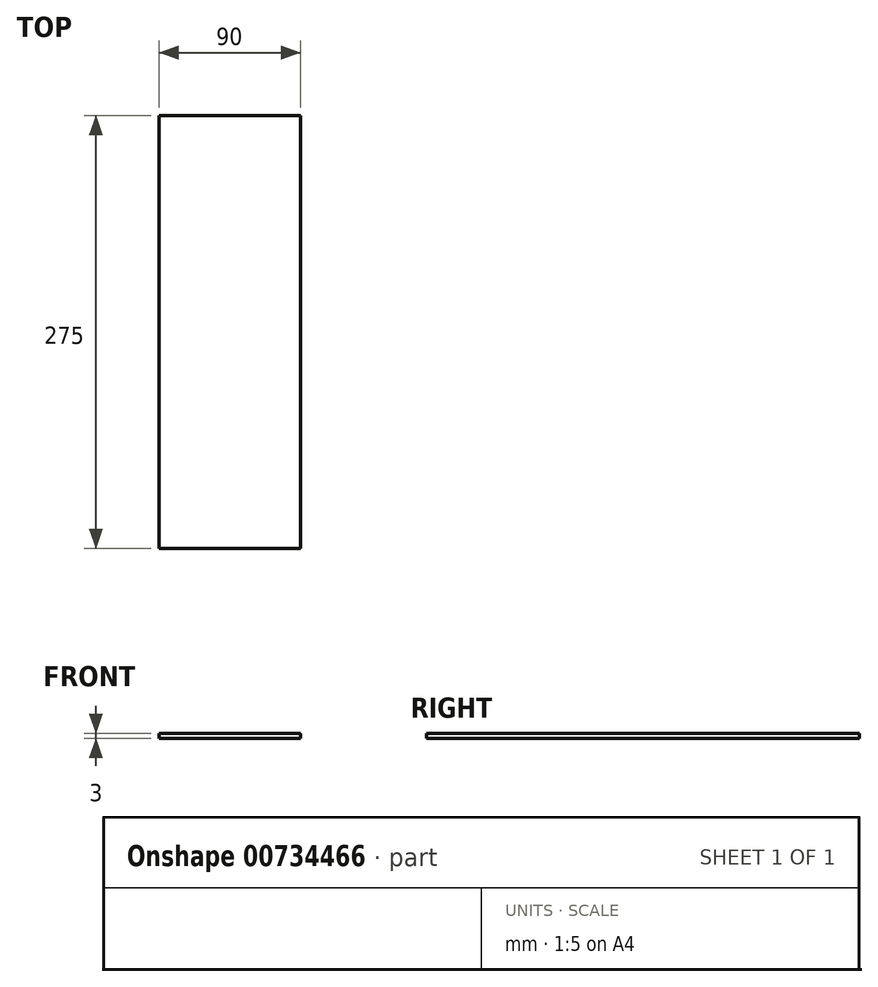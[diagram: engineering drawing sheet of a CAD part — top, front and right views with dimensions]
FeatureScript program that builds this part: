
annotation { "Feature Type Name" : "Feature", "Feature Type Description" : "" }
export const myFeature = defineFeature(function(context is Context, id is Id, definition is map)
    precondition{}
    {
        {
            var Q0;
            Q0=qCreatedBy(makeId("Front.planeOp"),FACE);
            var sketch = newSketch(context, id + "F0", { "sketchPlane" : qUnion([Q0])});
            skLineSegment(sketch, "E0", {"start": v(-50, 25) * mm, "end": v(50, 25) * mm});
            skLineSegment(sketch, "E1", {"start": v(50, 25) * mm, "end": v(50, -25) * mm});
            skLineSegment(sketch, "E2", {"start": v(-50, 25) * mm, "end": v(-50, -25) * mm});
            skSolve(sketch);
        }
        {
            var Q0;
            Q0=sQuery(id+"F0.wireOp",VERTEX,"E1.end");
            var Q1;
            Q1=qCreatedBy(makeId("Right.planeOp"),FACE);
            cPlane(context, id + "F1", {"entities" : qUnion([Q0, Q1]), "cplaneType" : CPlaneType.PLANE_POINT, "offset" : 25 * mm, "width" : 150 * mm, "height" : 150 * mm});
        }
        {
            var Q0;
            Q0=qCreatedBy(id+"F1.planeOp",FACE);
            var sketch = newSketch(context, id + "F2", { "sketchPlane" : qUnion([Q0])});
            skLineSegment(sketch, "E3", {"start": v(-20, -25) * mm, "end": v(20, -25) * mm});
            skSolve(sketch);
        }
        {
            var Q0;
            Q0=sQuery(id+"F0.wireOp",VERTEX,"E2.end");
            var Q1;
            Q1=qCreatedBy(makeId("Right.planeOp"),FACE);
            cPlane(context, id + "F3", {"entities" : qUnion([Q0, Q1]), "cplaneType" : CPlaneType.PLANE_POINT, "offset" : 25 * mm, "width" : 150 * mm, "height" : 150 * mm});
        }
        {
            var Q0;
            Q0=qCreatedBy(id+"F3.planeOp",FACE);
            var sketch = newSketch(context, id + "F4", { "sketchPlane" : qUnion([Q0])});
            skLineSegment(sketch, "E4", {"start": v(20, -25) * mm, "end": v(-20, -25) * mm});
            skLineSegment(sketch, "E5.bottom", {"start": v(1.5, 26.5) * mm, "end": v(-1.5, 26.5) * mm});
            skLineSegment(sketch, "E5.top", {"start": v(1.5, 23.5) * mm, "end": v(-1.5, 23.5) * mm});
            skLineSegment(sketch, "E5.left", {"start": v(1.5, 26.5) * mm, "end": v(1.5, 23.5) * mm});
            skLineSegment(sketch, "E5.right", {"start": v(-1.5, 26.5) * mm, "end": v(-1.5, 23.5) * mm});
            skSolve(sketch);
        }
        {
            var Q0;
            Q0=sQuery(id+"F4.wireOp",EDGE,"E5.right");
            var Q1;
            Q1=sQuery(id+"F4.wireOp",EDGE,"E5.left");
            var Q2;
            Q2=sQuery(id+"F4.wireOp",EDGE,"E5.top");
            var Q3;
            Q3=sQuery(id+"F4.wireOp",EDGE,"E5.bottom");
            extrude(context, id + "F5", {"bodyType" : ExtendedToolBodyType.SURFACE, "surfaceEntities" : qUnion([Q0, Q1, Q2, Q3]), "depth" : 219 * mm, "offsetDistance" : 25 * mm});
        }
        {
            var Q0;
            Q0=sQuery(id+"F0.wireOp",EDGE,"E1");
            extrude(context, id + "F6", {"bodyType" : ExtendedToolBodyType.SURFACE, "surfaceEntities" : qUnion([Q0]), "depth" : 227 * mm, "offsetDistance" : 25 * mm});
        }
        {
            var Q0;
            Q0=sQuery(id+"F2.wireOp",EDGE,"E3");
            var Q1;
            Q1=sQuery(id+"F4.wireOp",EDGE,"E5.top");
            extrude(context, id + "F7", {"bodyType" : ExtendedToolBodyType.SURFACE, "surfaceOperationType" : NewSurfaceOperationType.ADD, "surfaceEntities" : qUnion([Q0, Q1]), "depth" : 171 * mm, "offsetDistance" : 25 * mm});
        }
        {
            var Q0;
            Q0=sQuery(id+"F4.wireOp",EDGE,"E5.right");
            var Q1;
            Q1=sQuery(id+"F4.wireOp",VERTEX,"E5.top.start");
            extrude(context, id + "F8", {"bodyType" : ExtendedToolBodyType.SURFACE, "surfaceEntities" : qUnion([Q0]), "oppositeDirection" : true, "depth" : 90 * mm, "endBoundEntityVertex" : qUnion([Q1]), "offsetDistance" : 25 * mm});
        }
        {
            var Q0;
            Q0=makeQuery(id+"F8.opExtrude","SWEPT_FACE",FACE,{"disambiguationData":[OSD([sQuery(id+"F4.wireOp",EDGE,"E5.right")])]});
            extrude(context, id + "F9", {"entities" : qUnion([Q0]), "depth" : 68 * mm, "offsetDistance" : 25 * mm});
        }
        {
            var Q0;
            Q0=makeQuery(id+"F8.opExtrude","SWEPT_FACE",FACE,{"disambiguationData":[OSD([sQuery(id+"F4.wireOp",EDGE,"E5.right")])]});
            extrude(context, id + "F10", {"entities" : qUnion([Q0]), "operationType" : NewBodyOperationType.ADD, "oppositeDirection" : true, "depth" : 207 * mm, "offsetDistance" : 25 * mm});
        }
        {
            var Q0;
            Q0=sQuery(id+"F4.wireOp",EDGE,"E4");
            extrude(context, id + "F11", {"bodyType" : ExtendedToolBodyType.SURFACE, "surfaceEntities" : qUnion([Q0]), "depth" : 188 * mm, "offsetDistance" : 25 * mm});
        }
    });
